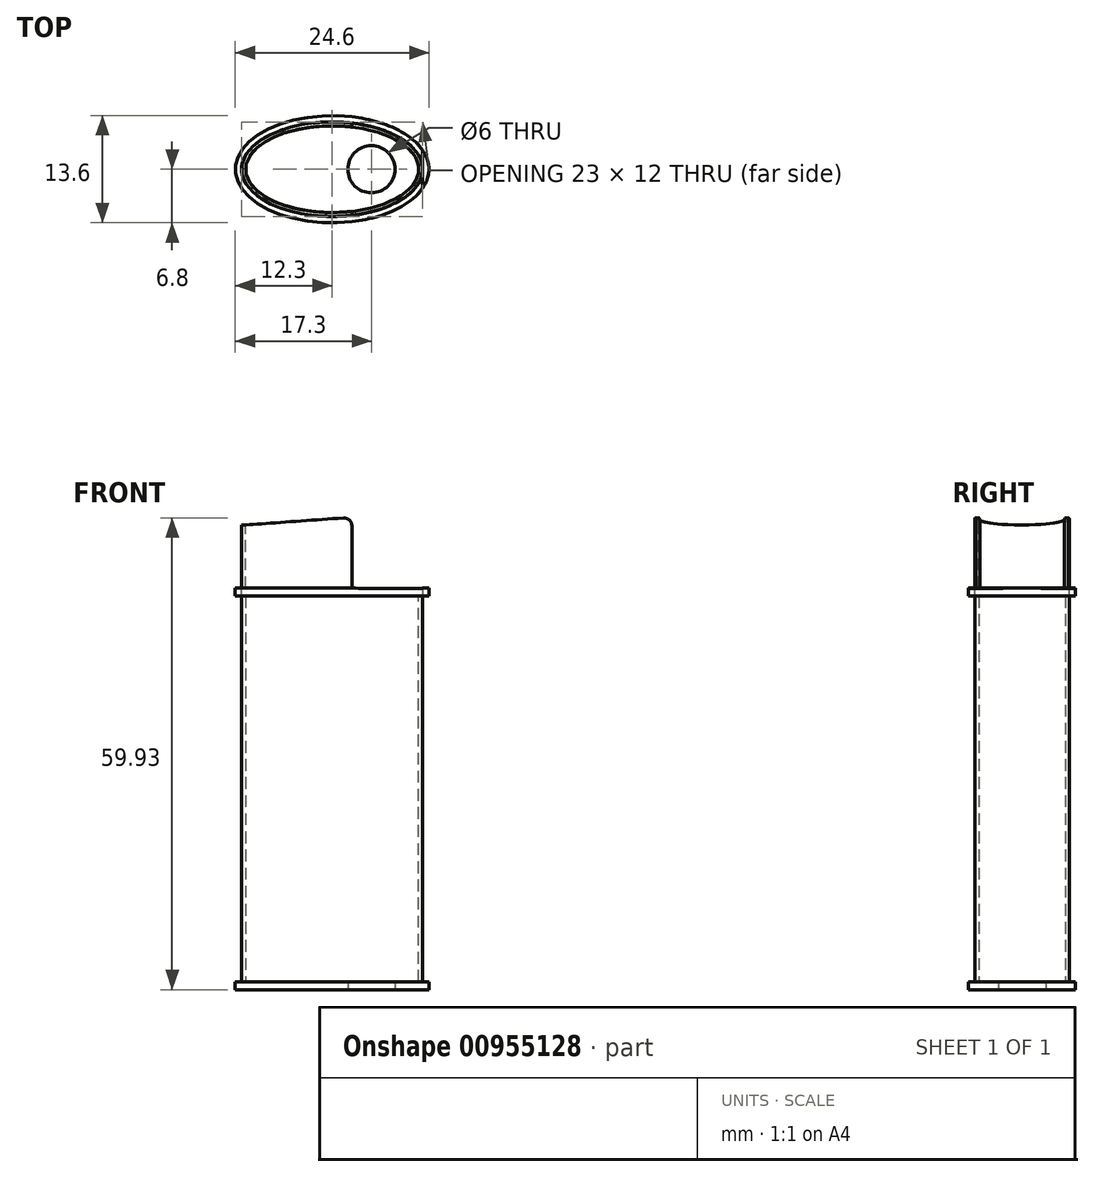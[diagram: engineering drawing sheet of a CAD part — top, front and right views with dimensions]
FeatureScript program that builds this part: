
annotation { "Feature Type Name" : "Feature", "Feature Type Description" : "" }
export const myFeature = defineFeature(function(context is Context, id is Id, definition is map)
    precondition{}
    {
        {
            var Q0;
            Q0=qCreatedBy(makeId("Top.planeOp"),FACE);
            var sketch = newSketch(context, id + "F0", { "sketchPlane" : qUnion([Q0])});
            skEllipse(sketch, "E0", {"center": v(0, 0) * mm, "majorRadius": 12.3 * mm, "minorRadius": 6.8 * mm, "majorAxis": v(1, 0)});
            skSolve(sketch);
        }
        {
            var Q0;
            Q0=makeQuery(id+"F0.imprint","IMPRINT",FACE,{"disambiguationData":[TD([[makeQuery(id+"F0.imprint","IMPRINT",EDGE,{"derivedFrom":sQuery(id+"F0.wireOp",EDGE,"E0")}),1.0]])]});
            extrude(context, id + "F1", {"entities" : qUnion([Q0]), "depth" : 50 * mm, "offsetDistance" : 25 * mm});
        }
        {
            var Q0;
            Q0=makeQuery(id+"F1.opExtrude","CAP_FACE",FACE,{"disambiguationData":[OSD([sQuery(id+"F0.wireOp",EDGE,"E0")])],"isStart":false});
            var sketch = newSketch(context, id + "F2", { "sketchPlane" : qUnion([Q0])});
            skEllipse(sketch, "E1", {"center": v(0, 0) * mm, "majorRadius": 11.5 * mm, "minorRadius": 6 * mm, "majorAxis": v(1, 0)});
            skSolve(sketch);
        }
        {
            var Q0;
            Q0=makeQuery(id+"F2.imprint","IMPRINT",FACE,{"disambiguationData":[TD([[makeQuery(id+"F2.imprint","IMPRINT",EDGE,{"derivedFrom":sQuery(id+"F2.wireOp",EDGE,"E1")}),-1.0]])]});
            extrude(context, id + "F3", {"entities" : qUnion([Q0]), "operationType" : NewBodyOperationType.REMOVE, "oppositeDirection" : true, "depth" : 49 * mm, "offsetDistance" : 25 * mm});
        }
        {
            var Q0;
            Q0=makeQuery(id+"F1.opExtrude","CAP_FACE",FACE,{"disambiguationData":[OSD([sQuery(id+"F0.wireOp",EDGE,"E0")])],"isStart":false});
            var sketch = newSketch(context, id + "F4", { "sketchPlane" : qUnion([Q0])});
            skEllipse(sketch, "E2", {"center": v(0, 0) * mm, "majorRadius": 12.3 * mm, "minorRadius": 6.8 * mm, "majorAxis": v(1, 0)});
            skSolve(sketch);
        }
        {
            var Q0;
            Q0=makeQuery(id+"F4.imprint","IMPRINT",FACE,{"disambiguationData":[TD([[makeQuery(id+"F4.imprint","IMPRINT",EDGE,{"derivedFrom":sQuery(id+"F4.wireOp",EDGE,"E2")}),1.0]])]});
            var Q1;
            Q1=makeQuery(id+"F4.imprint","IMPRINT",FACE,{"disambiguationData":[TD([[makeQuery(id+"F4.imprint","IMPRINT",EDGE,{"derivedFrom":makeQuery(id+"F3.boolean.opBoolean","COPY",EDGE,{"derivedFrom":makeQuery(id+"F3.opExtrude","CAP_EDGE",EDGE,{"disambiguationData":[OSD([sQuery(id+"F2.wireOp",EDGE,"E1")])],"isStart":true})})}),1.0]])]});
            var Q2;
            Q2=sQuery(id+"F4.wireOp",EDGE,"E2");
            extrude(context, id + "F5", {"entities" : qUnion([Q0, Q1]), "surfaceEntities" : qUnion([Q2]), "depth" : 1 * mm, "offsetDistance" : 25 * mm});
        }
        {
            var Q0;
            Q0=makeQuery(id+"F5.opExtrude","CAP_FACE",FACE,{"disambiguationData":[OSD([sQuery(id+"F4.wireOp",EDGE,"E2")])],"isStart":false});
            var sketch = newSketch(context, id + "F6", { "sketchPlane" : qUnion([Q0])});
            skEllipse(sketch, "E3", {"center": v(0, 0) * mm, "majorRadius": 11.5 * mm, "minorRadius": 6 * mm, "majorAxis": v(1, 0)});
            skSolve(sketch);
        }
        {
            var Q0;
            Q0=makeQuery(id+"F6.imprint","IMPRINT",FACE,{"disambiguationData":[TD([[makeQuery(id+"F6.imprint","IMPRINT",EDGE,{"derivedFrom":sQuery(id+"F6.wireOp",EDGE,"E3")}),1.0]])]});
            extrude(context, id + "F7", {"entities" : qUnion([Q0]), "operationType" : NewBodyOperationType.ADD, "depth" : 9 * mm, "offsetDistance" : 25 * mm});
        }
        {
            var Q0;
            Q0=makeQuery(id+"F7.opExtrude","CAP_FACE",FACE,{"disambiguationData":[OSD([sQuery(id+"F6.wireOp",EDGE,"E3")])],"isStart":false});
            var sketch = newSketch(context, id + "F8", { "sketchPlane" : qUnion([Q0])});
            skEllipse(sketch, "E4", {"center": v(0, 0) * mm, "majorRadius": 11 * mm, "minorRadius": 5.5 * mm, "majorAxis": v(1, 0)});
            skSolve(sketch);
        }
        {
            var Q0;
            Q0 = qSketchRegion(id + "F8", true);
            extrude(context, id + "F9", {"entities" : qUnion([Q0]), "operationType" : NewBodyOperationType.REMOVE, "oppositeDirection" : true, "depth" : 59 * mm, "offsetDistance" : 25 * mm});
        }
        {
            var Q0;
            Q0=qCreatedBy(makeId("Front.planeOp"),FACE);
            var sketch = newSketch(context, id + "F10", { "sketchPlane" : qUnion([Q0])});
            skLineSegment(sketch, "E5", {"start": v(0, 51) * mm, "end": v(2.5, 51) * mm});
            skLineSegment(sketch, "E6", {"start": v(2.5, 51) * mm, "end": v(2.5, 58.93) * mm});
            skLineSegment(sketch, "E7", {"start": v(-11.5, 59) * mm, "end": v(1.43, 59.92) * mm});
            skLineSegment(sketch, "E8", {"start": v(-11.5, 59) * mm, "end": v(-11.5, 51) * mm});
            skPoint(sketch, "E9.visualSharp", {"position": v(2.5, 60) * mm});
            skArc(sketch, "E9.filletArc", {"start": v(2.5, 58.93) * mm, "mid": v(2.18, 59.66) * mm, "end": v(1.43, 59.92) * mm});
            skLineSegment(sketch, "E10", {"start": v(-11.5, 59) * mm, "end": v(-11.5, 60.1) * mm});
            skLineSegment(sketch, "E11", {"start": v(-11.5, 60.1) * mm, "end": v(11.5, 60.1) * mm});
            skLineSegment(sketch, "E12", {"start": v(11.5, 60.1) * mm, "end": v(11.5, 50.97) * mm});
            skLineSegment(sketch, "E13", {"start": v(11.5, 50.97) * mm, "end": v(2.5, 51) * mm});
            skSolve(sketch);
        }
        {
            var Q0;
            Q0 = qSketchRegion(id + "F10", true);
            extrude(context, id + "F11", {"entities" : qUnion([Q0]), "operationType" : NewBodyOperationType.REMOVE, "endBound" : BoundingType.SYMMETRIC, "oppositeDirection" : true, "depth" : 25 * mm, "offsetDistance" : 25 * mm});
        }
        {
            var Q0;
            Q0=makeQuery(id+"F1.opExtrude","CAP_FACE",FACE,{"disambiguationData":[OSD([sQuery(id+"F0.wireOp",EDGE,"E0")])],"isStart":true});
            var sketch = newSketch(context, id + "F12", { "sketchPlane" : qUnion([Q0])});
            skCircle(sketch, "E14", {"center": v(5, 0) * mm, "radius": 3 * mm});
            skSolve(sketch);
        }
        {
            var Q0;
            Q0 = qSketchRegion(id + "F12", true);
            extrude(context, id + "F13", {"entities" : qUnion([Q0]), "operationType" : NewBodyOperationType.REMOVE, "oppositeDirection" : true, "depth" : 61 * mm, "offsetDistance" : 25 * mm});
        }
        {
            var Q0;
            Q0=makeQuery(id+"F1.opExtrude","CAP_FACE",FACE,{"disambiguationData":[OSD([sQuery(id+"F0.wireOp",EDGE,"E0")])],"isStart":false});
            var sketch = newSketch(context, id + "F14", { "sketchPlane" : qUnion([Q0])});
            skEllipse(sketch, "E15", {"center": v(0, 0) * mm, "majorRadius": 11 * mm, "minorRadius": 5.5 * mm, "majorAxis": v(1, 0)});
            skSolve(sketch);
        }
        {
            var Q0;
            Q0 = qSketchRegion(id + "F14", true);
            extrude(context, id + "F15", {"entities" : qUnion([Q0]), "operationType" : NewBodyOperationType.REMOVE, "oppositeDirection" : true, "depth" : 49 * mm, "offsetDistance" : 25 * mm});
        }
    });
